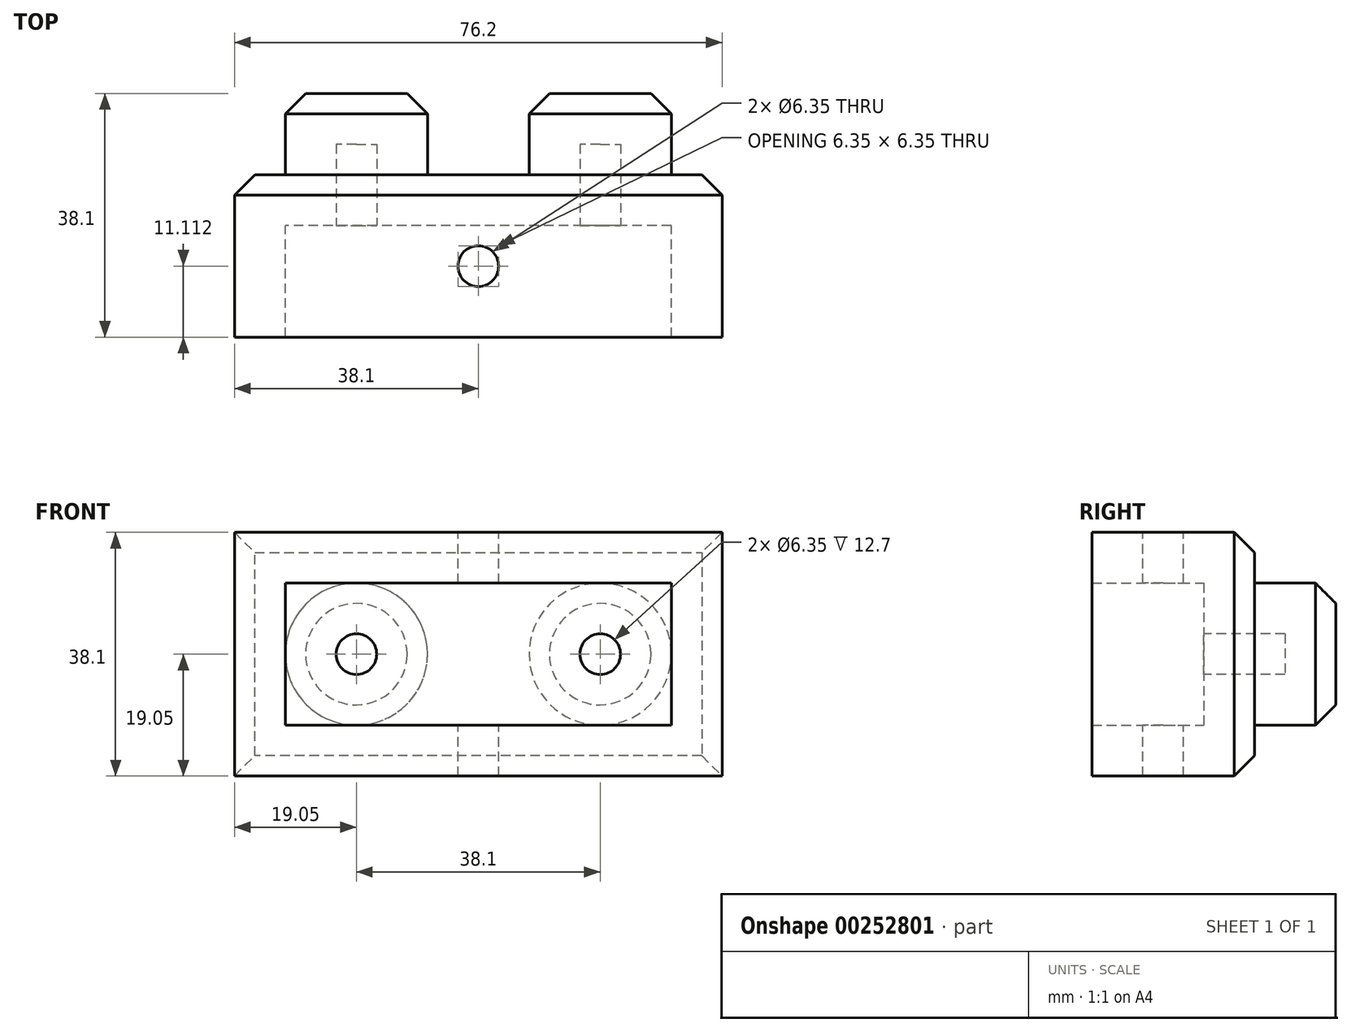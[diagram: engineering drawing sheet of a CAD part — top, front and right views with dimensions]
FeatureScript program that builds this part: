
annotation { "Feature Type Name" : "Feature", "Feature Type Description" : "" }
export const myFeature = defineFeature(function(context is Context, id is Id, definition is map)
    precondition{}
    {
        {
            var Q0;
            Q0=qCreatedBy(makeId("Front.planeOp"),FACE);
            var sketch = newSketch(context, id + "F0", { "sketchPlane" : qUnion([Q0])});
            skLineSegment(sketch, "E0.bottom", {"start": v(38.1, -19.05) * mm, "end": v(-38.1, -19.05) * mm});
            skLineSegment(sketch, "E0.top", {"start": v(38.1, 19.05) * mm, "end": v(-38.1, 19.05) * mm});
            skLineSegment(sketch, "E0.left", {"start": v(38.1, -19.05) * mm, "end": v(38.1, 19.05) * mm});
            skLineSegment(sketch, "E0.right", {"start": v(-38.1, -19.05) * mm, "end": v(-38.1, 19.05) * mm});
            skPoint(sketch, "E0.middle", {"position": v(0, 0) * mm});
            skSolve(sketch);
        }
        {
            var Q0;
            Q0 = qSketchRegion(id + "F0", true);
            extrude(context, id + "F1", {"entities" : qUnion([Q0]), "depth" : 25.4 * mm});
        }
        {
            var Q0;
            Q0=makeQuery(id+"F1.opExtrude","CAP_FACE",FACE,{"disambiguationData":[OSD([sQuery(id+"F0.wireOp",EDGE,"E0.bottom"),sQuery(id+"F0.wireOp",EDGE,"E0.top"),sQuery(id+"F0.wireOp",EDGE,"E0.left"),sQuery(id+"F0.wireOp",EDGE,"E0.right")])],"isStart":true});
            var sketch = newSketch(context, id + "F2", { "sketchPlane" : qUnion([Q0])});
            skCircle(sketch, "E1", {"center": v(-19.05, 0) * mm, "radius": 11.11 * mm});
            skCircle(sketch, "E2", {"center": v(19.05, 0) * mm, "radius": 11.11 * mm});
            skSolve(sketch);
        }
        {
            var Q0;
            Q0=makeQuery(id+"F2.imprint","IMPRINT",FACE,{"disambiguationData":[TD([[makeQuery(id+"F2.imprint","IMPRINT",EDGE,{"derivedFrom":sQuery(id+"F2.wireOp",EDGE,"E1")}),1.0]])]});
            var Q1;
            Q1=makeQuery(id+"F2.imprint","IMPRINT",FACE,{"disambiguationData":[TD([[makeQuery(id+"F2.imprint","IMPRINT",EDGE,{"derivedFrom":sQuery(id+"F2.wireOp",EDGE,"E2")}),1.0]])]});
            extrude(context, id + "F3", {"entities" : qUnion([Q0, Q1]), "operationType" : NewBodyOperationType.ADD, "depth" : 12.7 * mm});
        }
        {
            var Q0;
            Q0=makeQuery(id+"F3.opExtrude","CAP_EDGE",EDGE,{"disambiguationData":[OSD([sQuery(id+"F2.wireOp",EDGE,"E1")])],"isStart":false});
            var Q1;
            Q1=makeQuery(id+"F3.opExtrude","CAP_EDGE",EDGE,{"disambiguationData":[OSD([sQuery(id+"F2.wireOp",EDGE,"E2")])],"isStart":false});
            chamfer(context, id + "F4", {"entities" : qUnion([Q0, Q1]), "chamferType" : ChamferType.OFFSET_ANGLE, "width" : 3.17 * mm, "oppositeDirection" : false, "angle" : 45 * degree, "tangentPropagation" : true});
        }
        {
            var Q0;
            Q0=makeQuery(id+"F1.opExtrude","CAP_EDGE",EDGE,{"disambiguationData":[OSD([sQuery(id+"F0.wireOp",EDGE,"E0.top")])],"isStart":true});
            var Q1;
            Q1=makeQuery(id+"F1.opExtrude","CAP_EDGE",EDGE,{"disambiguationData":[OSD([sQuery(id+"F0.wireOp",EDGE,"E0.left")])],"isStart":true});
            var Q2;
            Q2=makeQuery(id+"F1.opExtrude","CAP_EDGE",EDGE,{"disambiguationData":[OSD([sQuery(id+"F0.wireOp",EDGE,"E0.bottom")])],"isStart":true});
            var Q3;
            Q3=makeQuery(id+"F1.opExtrude","CAP_EDGE",EDGE,{"disambiguationData":[OSD([sQuery(id+"F0.wireOp",EDGE,"E0.right")])],"isStart":true});
            chamfer(context, id + "F5", {"entities" : qUnion([Q0, Q1, Q2, Q3]), "chamferType" : ChamferType.OFFSET_ANGLE, "width" : 3.17 * mm, "oppositeDirection" : false, "angle" : 45 * degree, "tangentPropagation" : true});
        }
        {
            var Q0;
            Q0=makeQuery(id+"F1.opExtrude","CAP_FACE",FACE,{"disambiguationData":[OSD([sQuery(id+"F0.wireOp",EDGE,"E0.bottom"),sQuery(id+"F0.wireOp",EDGE,"E0.top"),sQuery(id+"F0.wireOp",EDGE,"E0.left"),sQuery(id+"F0.wireOp",EDGE,"E0.right")])],"isStart":false});
            shell(context, id + "F6", {"entities" : qUnion([Q0]), "thickness" : 7.94 * mm});
        }
        {
            var Q0;
            Q0=makeQuery(id+"F1.opExtrude","SWEPT_FACE",FACE,{"disambiguationData":[OSD([sQuery(id+"F0.wireOp",EDGE,"E0.top")])]});
            var sketch = newSketch(context, id + "F7", { "sketchPlane" : qUnion([Q0])});
            skCircle(sketch, "E3", {"center": v(0, -14.29) * mm, "radius": 3.18 * mm});
            skSolve(sketch);
        }
        {
            var Q0;
            Q0 = qSketchRegion(id + "F7", true);
            extrude(context, id + "F8", {"entities" : qUnion([Q0]), "operationType" : NewBodyOperationType.REMOVE, "oppositeDirection" : true, "depth" : 38.1 * mm});
        }
    });
